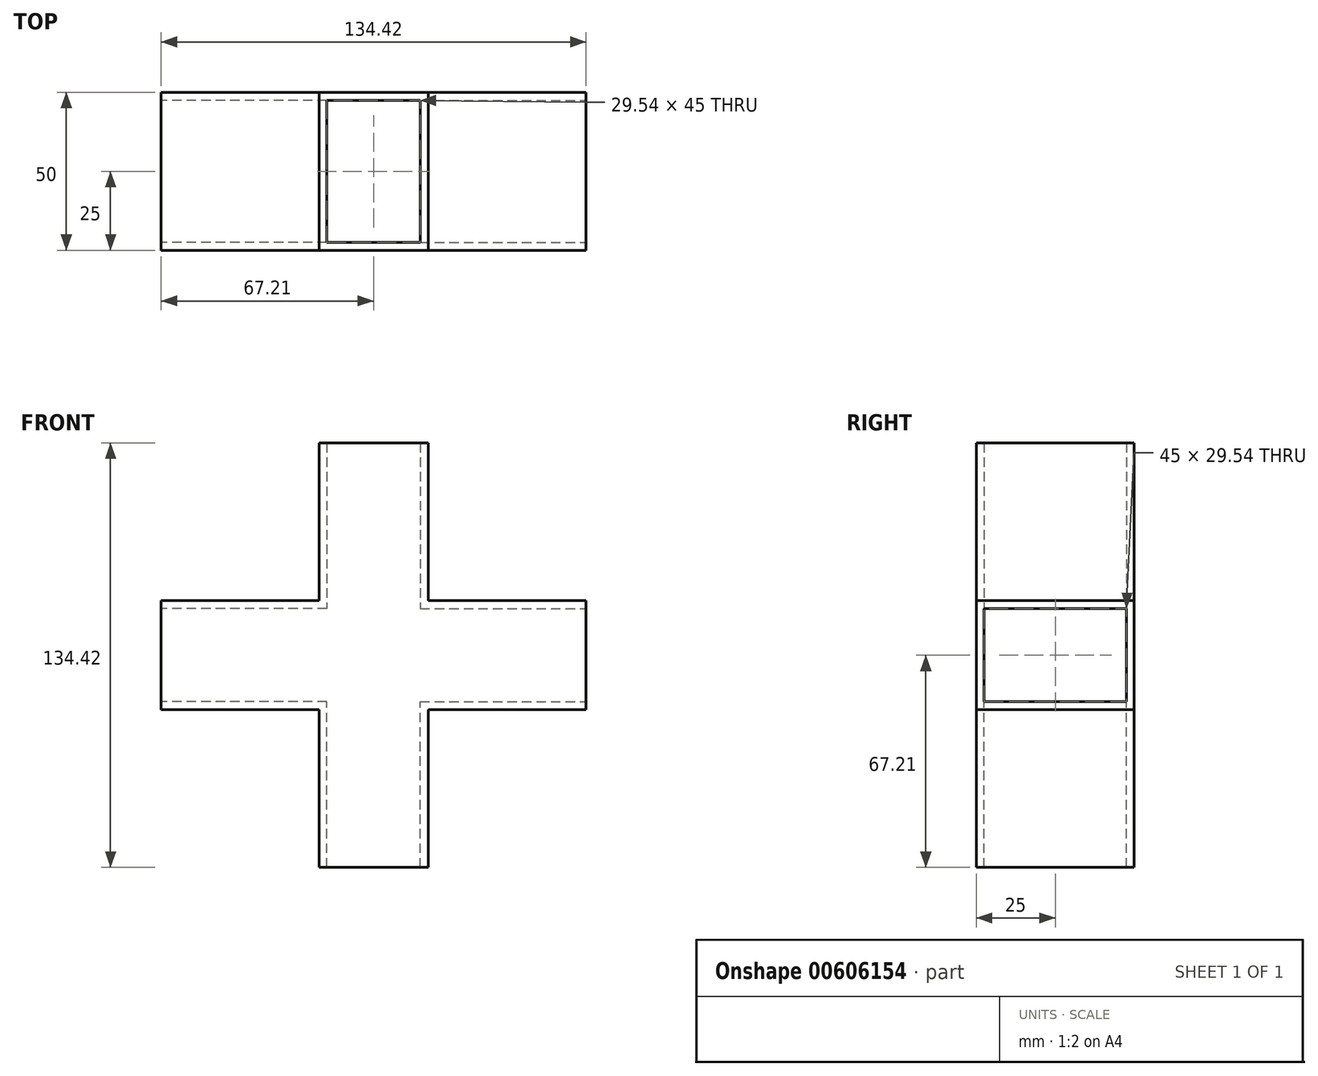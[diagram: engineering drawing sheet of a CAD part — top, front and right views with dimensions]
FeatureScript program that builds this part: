
annotation { "Feature Type Name" : "Feature", "Feature Type Description" : "" }
export const myFeature = defineFeature(function(context is Context, id is Id, definition is map)
    precondition{}
    {
        {
            var Q0;
            Q0=qCreatedBy(makeId("Front.planeOp"),FACE);
            var sketch = newSketch(context, id + "F0", { "sketchPlane" : qUnion([Q0])});
            skLineSegment(sketch, "E0", {"start": v(0, 67.21) * mm, "end": v(-17.27, 67.21) * mm});
            skLineSegment(sketch, "E1", {"start": v(-17.27, 67.21) * mm, "end": v(-17.27, 17.27) * mm});
            skLineSegment(sketch, "E2", {"start": v(-17.27, 17.27) * mm, "end": v(-67.21, 17.27) * mm});
            skLineSegment(sketch, "E3", {"start": v(-67.21, 17.27) * mm, "end": v(-67.21, 0) * mm});
            skLineSegment(sketch, "E4", {"start": v(17.64, 0) * mm, "end": v(0, 0) * mm, "construction": true});
            skLineSegment(sketch, "E5", {"start": v(0, 0) * mm, "end": v(0, -21.17) * mm, "construction": true});
            skLineSegment(sketch, "E6.MirrorCS", {"start": v(0, 67.21) * mm, "end": v(17.27, 67.21) * mm});
            skLineSegment(sketch, "E7.MirrorCS", {"start": v(17.27, 17.27) * mm, "end": v(67.21, 17.27) * mm});
            skLineSegment(sketch, "E8.MirrorCS", {"start": v(67.21, 17.27) * mm, "end": v(67.21, 0) * mm});
            skLineSegment(sketch, "E9.MirrorCS", {"start": v(17.27, 67.21) * mm, "end": v(17.27, 17.27) * mm});
            skLineSegment(sketch, "E10.MirrorCS", {"start": v(17.27, -67.21) * mm, "end": v(17.27, -17.27) * mm});
            skLineSegment(sketch, "E11.MirrorCS", {"start": v(67.21, -17.27) * mm, "end": v(67.21, 0) * mm});
            skLineSegment(sketch, "E12.MirrorCS", {"start": v(17.27, -17.27) * mm, "end": v(67.21, -17.27) * mm});
            skLineSegment(sketch, "E13.MirrorCS", {"start": v(-67.21, -17.27) * mm, "end": v(-67.21, 0) * mm});
            skLineSegment(sketch, "E14.MirrorCS", {"start": v(-17.27, -17.27) * mm, "end": v(-67.21, -17.27) * mm});
            skLineSegment(sketch, "E15.MirrorCS", {"start": v(0, -67.21) * mm, "end": v(17.27, -67.21) * mm});
            skLineSegment(sketch, "E16.MirrorCS", {"start": v(0, -67.21) * mm, "end": v(-17.27, -67.21) * mm});
            skLineSegment(sketch, "E17.MirrorCS", {"start": v(-17.27, -67.21) * mm, "end": v(-17.27, -17.27) * mm});
            skSolve(sketch);
        }
        {
            var Q0;
            Q0=qSketchRegion(id+"F0",true);
            extrude(context, id + "F1", {"entities" : qUnion([Q0]), "depth" : 50 * mm, "offsetDistance" : 25 * mm});
        }
        {
            var Q0;
            Q0=makeQuery(id+"F1.opExtrude","SWEPT_FACE",FACE,{"disambiguationData":[OSD([sQuery(id+"F0.wireOp",EDGE,"E8.MirrorCS"),sQuery(id+"F0.wireOp",EDGE,"E11.MirrorCS")])]});
            var Q1;
            Q1=makeQuery(id+"F1.opExtrude","SWEPT_FACE",FACE,{"disambiguationData":[OSD([sQuery(id+"F0.wireOp",EDGE,"E0"),sQuery(id+"F0.wireOp",EDGE,"E6.MirrorCS")])]});
            var Q2;
            Q2=makeQuery(id+"F1.opExtrude","SWEPT_FACE",FACE,{"disambiguationData":[OSD([sQuery(id+"F0.wireOp",EDGE,"E3"),sQuery(id+"F0.wireOp",EDGE,"E13.MirrorCS")])]});
            var Q3;
            Q3=makeQuery(id+"F1.opExtrude","SWEPT_FACE",FACE,{"disambiguationData":[OSD([sQuery(id+"F0.wireOp",EDGE,"E15.MirrorCS"),sQuery(id+"F0.wireOp",EDGE,"E16.MirrorCS")])]});
            shell(context, id + "F2", {"entities" : qUnion([Q0, Q1, Q2, Q3]), "thickness" : 2.5 * mm});
        }
    });
